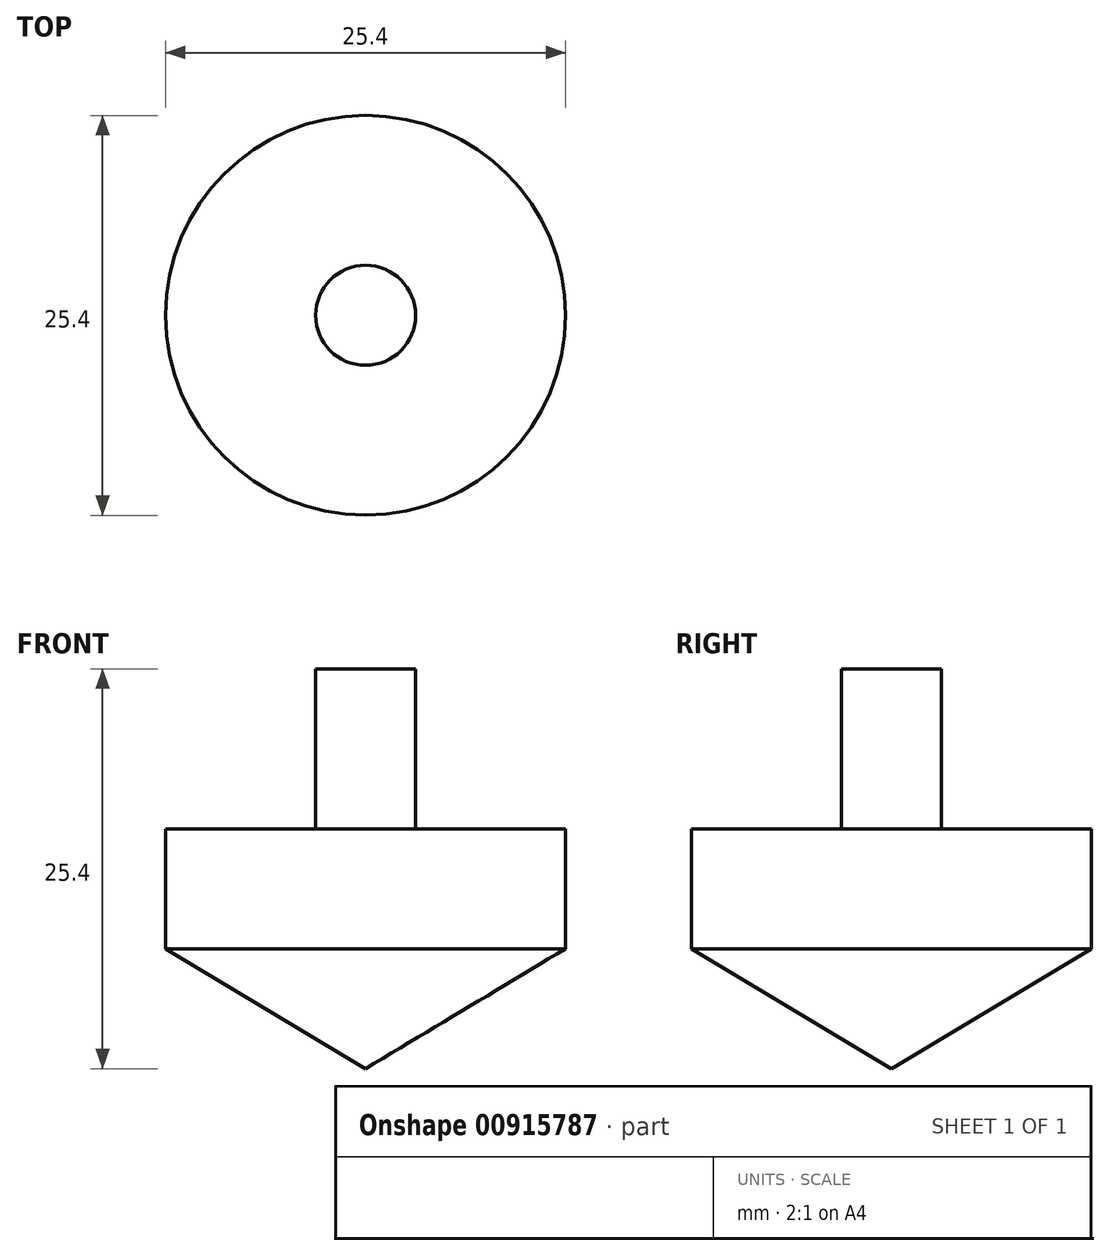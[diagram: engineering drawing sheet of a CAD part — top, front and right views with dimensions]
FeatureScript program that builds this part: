
annotation { "Feature Type Name" : "Feature", "Feature Type Description" : "" }
export const myFeature = defineFeature(function(context is Context, id is Id, definition is map)
    precondition{}
    {
        {
            var Q0;
            Q0=qCreatedBy(makeId("Top.planeOp"),FACE);
            var sketch = newSketch(context, id + "F0", { "sketchPlane" : qUnion([Q0])});
            skCircle(sketch, "E0", {"center": v(-52.36, 15.36) * mm, "radius": 12.7 * mm});
            skSolve(sketch);
        }
        {
            var Q0;
            Q0=makeQuery(id+"F0.imprint","IMPRINT",FACE,{"disambiguationData":[TD([[makeQuery(id+"F0.imprint","IMPRINT",EDGE,{"derivedFrom":sQuery(id+"F0.wireOp",EDGE,"E0")}),1.0]])]});
            extrude(context, id + "F1", {"entities" : qUnion([Q0]), "depth" : 15.24 * mm, "offsetDistance" : 25.4 * mm});
        }
        {
            var Q0;
            Q0=makeQuery(id+"F1.opExtrude","CAP_EDGE",EDGE,{"disambiguationData":[OSD([sQuery(id+"F0.wireOp",EDGE,"E0")])],"isStart":true});
            chamfer(context, id + "F2", {"entities" : qUnion([Q0]), "chamferType" : ChamferType.TWO_OFFSETS, "width1" : 7.62 * mm, "oppositeDirection" : false, "width2" : 12.7 * mm, "tangentPropagation" : true});
        }
        {
            var Q0;
            Q0=makeQuery(id+"F1.opExtrude","CAP_FACE",FACE,{"disambiguationData":[OSD([sQuery(id+"F0.wireOp",EDGE,"E0")])],"isStart":false});
            cPlane(context, id + "F3", {"entities" : qUnion([Q0]), "cplaneType" : CPlaneType.OFFSET, "offset" : 10.16 * mm, "width" : 152.4 * mm, "height" : 152.4 * mm});
        }
        {
            var Q0;
            Q0=makeQuery(id+"F1.opExtrude","CAP_FACE",FACE,{"disambiguationData":[OSD([sQuery(id+"F0.wireOp",EDGE,"E0")])],"isStart":false});
            var sketch = newSketch(context, id + "F4", { "sketchPlane" : qUnion([Q0])});
            skCircle(sketch, "E1", {"center": v(-52.36, 15.36) * mm, "radius": 12.7 * mm});
            skPoint(sketch, "E1.first.point", {"position": v(-44.4, 25.26) * mm});
            skPoint(sketch, "E1.second.point", {"position": v(-62.22, 7.36) * mm});
            skPoint(sketch, "E1.third.point", {"position": v(-51.77, 2.68) * mm});
            skCircle(sketch, "E2", {"center": v(-52.36, 15.36) * mm, "radius": 3.18 * mm});
            skSolve(sketch);
        }
        {
            var Q0;
            Q0=qCreatedBy(id+"F3.planeOp",FACE);
            var sketch = newSketch(context, id + "F5", { "sketchPlane" : qUnion([Q0])});
            skPoint(sketch, "E3", {"position": v(-52.36, 15.36) * mm});
            skCircle(sketch, "E4", {"center": v(-52.36, 15.36) * mm, "radius": 3.17 * mm});
            skSolve(sketch);
        }
        {
            var Q1;
            Q1=makeQuery(id+"F4.imprint","IMPRINT",FACE,{"disambiguationData":[TD([[makeQuery(id+"F4.imprint","IMPRINT",EDGE,{"derivedFrom":sQuery(id+"F4.wireOp",EDGE,"E2")}),1.0]])]});
            var Q2;
            Q2=makeQuery(id+"F5.imprint","IMPRINT",FACE,{"disambiguationData":[TD([[makeQuery(id+"F5.imprint","IMPRINT",EDGE,{"derivedFrom":sQuery(id+"F5.wireOp",EDGE,"E4")}),1.0]])]});
            loft(context, id + "F6", {"operationType" : NewBodyOperationType.ADD, "sheetProfilesArray" : [{ "sheetProfileEntities" : qUnion([Q1]) }, { "sheetProfileEntities" : qUnion([Q2]) }]});
        }
    });
